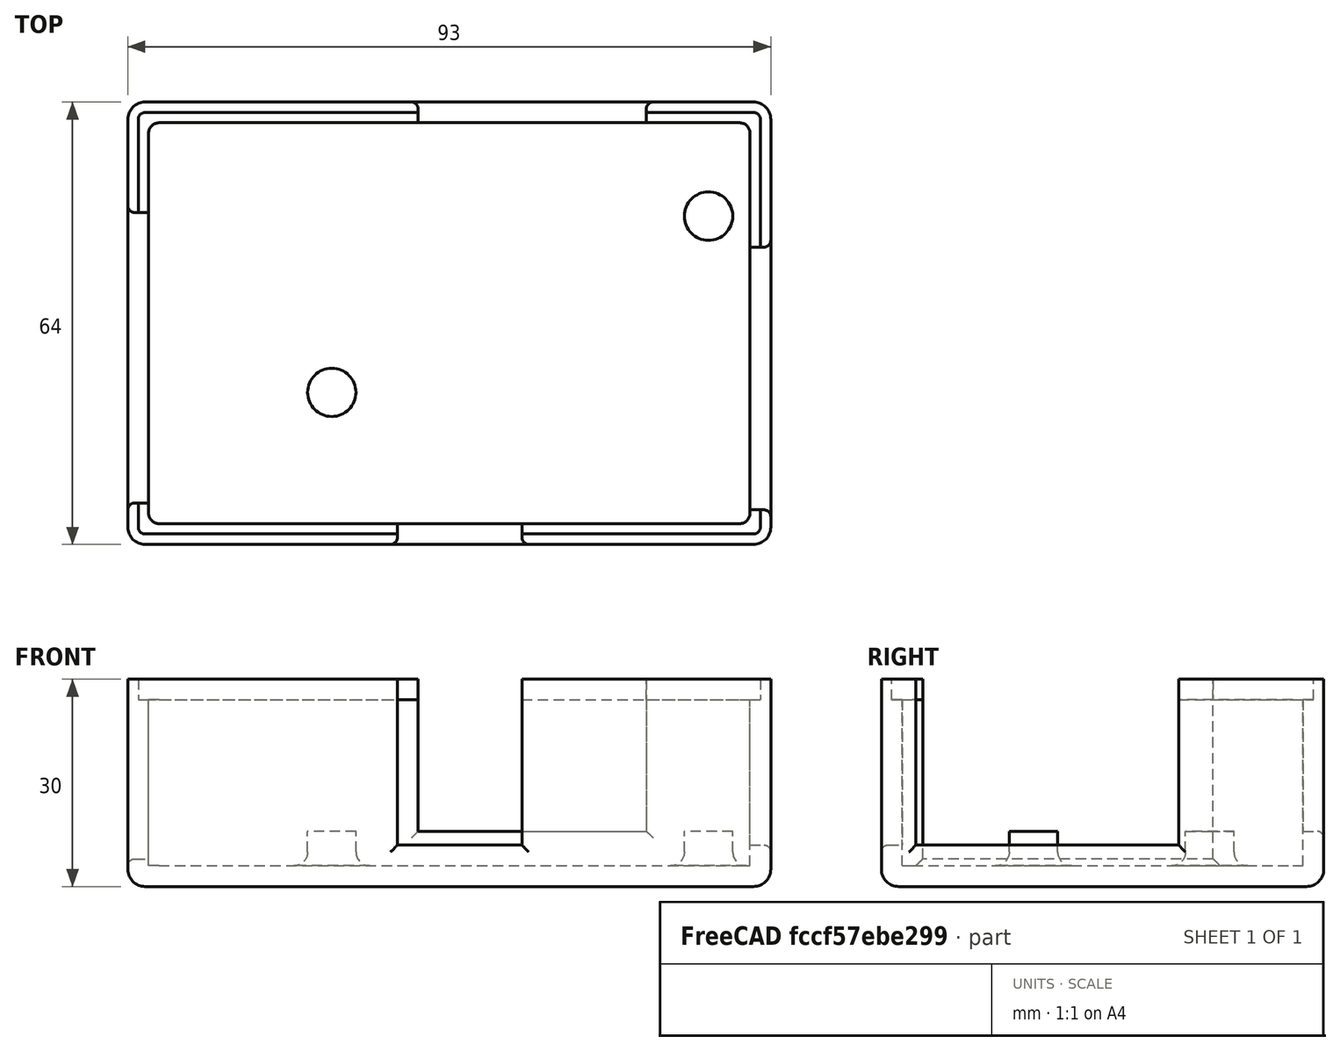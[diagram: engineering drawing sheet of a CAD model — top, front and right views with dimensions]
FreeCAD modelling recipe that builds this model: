
FCSTD DOCUMENT
Label: PiCase_Step_06
objects: PartDesign::Fillet×9, Part::Feature×1
note: 10 computed .brp shape members not serialized (recipe doc carries the construction recipe); baked Part::Feature solids carry a one-line shape summary decoded from their .brp

FEATURE [Part::Feature] Shape
  shape: bbox 93 x 64 x 30 mm, 42 faces (baked)
FEATURE [PartDesign::Fillet] Fillet
  Base = -> Shape [Edge9,Edge1,Edge4,Edge21,Edge3,Edge13,Edge2,Edge8]
  Radius = 2.5
FEATURE [PartDesign::Fillet] Fillet001
  Base = -> Fillet [Edge42,Edge40,Edge39]
  Radius = 1
FEATURE [PartDesign::Fillet] Fillet002
  Base = -> Fillet001 [Edge39,Edge41,Edge43]
  Radius = 1
FEATURE [PartDesign::Fillet] Fillet003
  Base = -> Fillet002 [Edge94,Edge92,Edge96]
  Radius = 1
FEATURE [PartDesign::Fillet] Fillet004
  Base = -> Fillet003 [Edge59,Edge83,Edge110,Edge61]
  Radius = 1.5
FEATURE [PartDesign::Fillet] Fillet005
  Base = -> Fillet004 [Edge145,Edge71,Edge68,Edge137]
  Radius = 1
FEATURE [PartDesign::Fillet] Fillet006
  Base = -> Fillet005 [Edge52]
  Radius = 2
FEATURE [PartDesign::Fillet] Fillet007
  Base = -> Fillet006 [Edge10]
  Radius = 2
FEATURE [PartDesign::Fillet] Fillet008
  Base = -> Fillet007 [Edge100,Edge106,Edge104]
  Radius = 1
